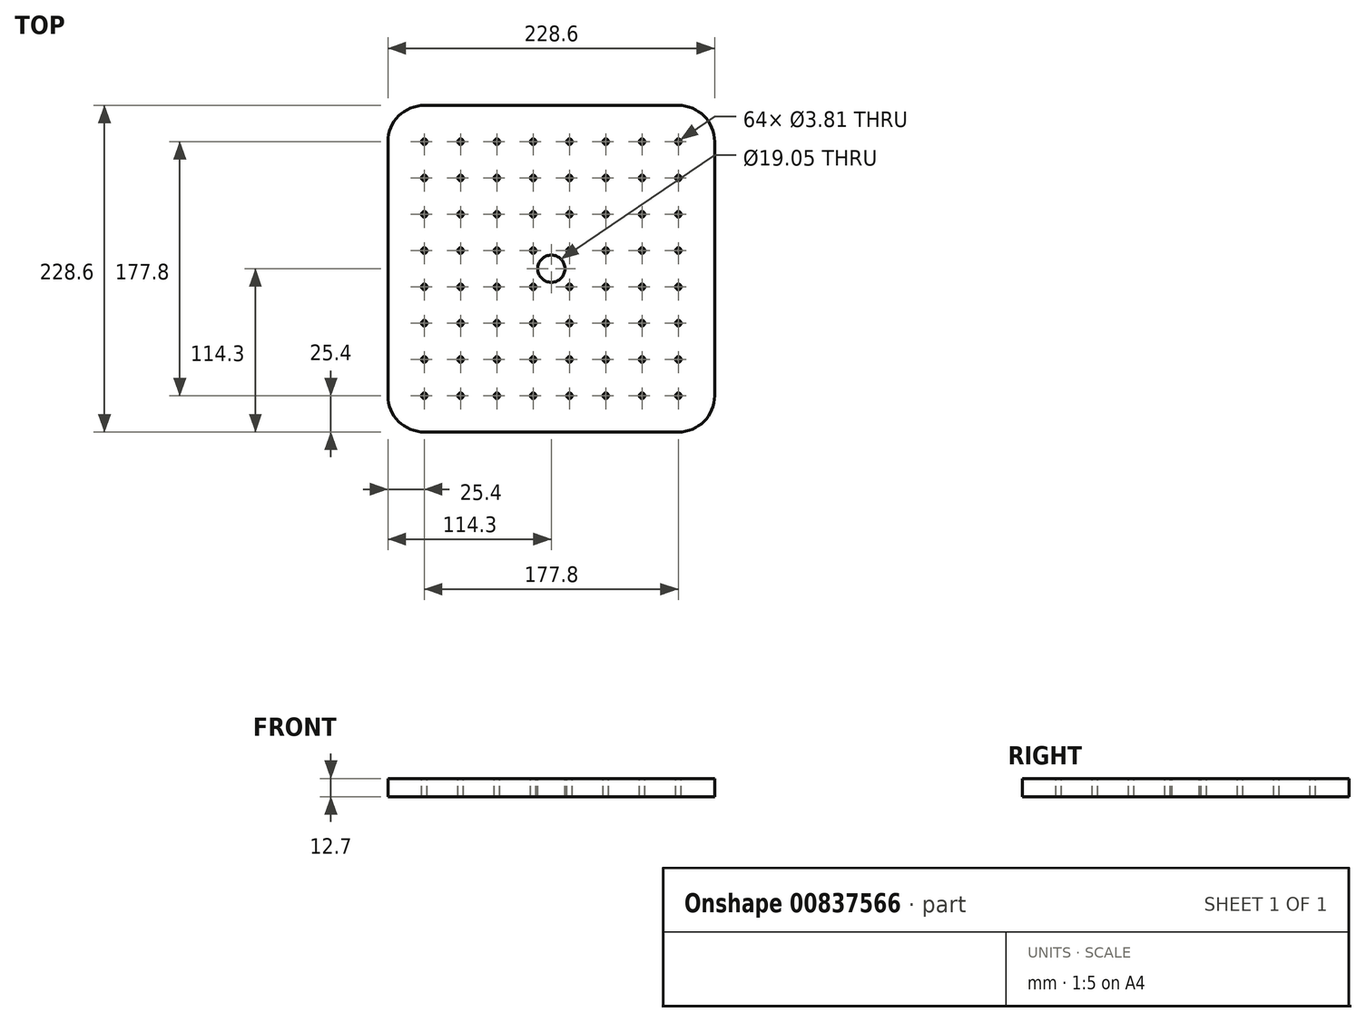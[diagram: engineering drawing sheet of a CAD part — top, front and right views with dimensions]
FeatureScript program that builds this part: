
annotation { "Feature Type Name" : "Feature", "Feature Type Description" : "" }
export const myFeature = defineFeature(function(context is Context, id is Id, definition is map)
    precondition{}
    {
        {
            var Q0;
            Q0=qCreatedBy(makeId("Top.planeOp"),FACE);
            var sketch = newSketch(context, id + "F0", { "sketchPlane" : qUnion([Q0])});
            skLineSegment(sketch, "E0.bottom", {"start": v(88.9, 114.3) * mm, "end": v(-88.9, 114.3) * mm});
            skLineSegment(sketch, "E0.top", {"start": v(88.9, -114.3) * mm, "end": v(-88.9, -114.3) * mm});
            skLineSegment(sketch, "E0.left", {"start": v(114.3, 88.9) * mm, "end": v(114.3, -88.9) * mm});
            skLineSegment(sketch, "E0.right", {"start": v(-114.3, 88.9) * mm, "end": v(-114.3, -88.9) * mm});
            skPoint(sketch, "E0.middle", {"position": v(0, 0) * mm});
            skCircle(sketch, "E1", {"center": v(-88.9, 88.9) * mm, "radius": 1.9 * mm});
            skLineSegment(sketch, "E2", {"start": v(-88.9, 88.9) * mm, "end": v(-88.9, 114.3) * mm, "construction": true});
            skLineSegment(sketch, "E3", {"start": v(-114.3, 88.9) * mm, "end": v(-88.9, 88.9) * mm, "construction": true});
            skCircle(sketch, "E4.0.1.0", {"center": v(-88.9, 63.5) * mm, "radius": 1.9 * mm});
            skCircle(sketch, "E4.1.0.0", {"center": v(-63.5, 88.9) * mm, "radius": 1.9 * mm});
            skCircle(sketch, "E4.1.1.0", {"center": v(-63.5, 63.5) * mm, "radius": 1.9 * mm});
            skCircle(sketch, "E4.2.0.0", {"center": v(-38.1, 88.9) * mm, "radius": 1.9 * mm});
            skCircle(sketch, "E4.2.1.0", {"center": v(-38.1, 63.5) * mm, "radius": 1.9 * mm});
            skLineSegment(sketch, "E4.direction1", {"start": v(-88.9, 88.9) * mm, "end": v(-63.5, 88.9) * mm, "construction": true});
            skLineSegment(sketch, "E4.direction2", {"start": v(-88.9, 88.9) * mm, "end": v(-88.9, 63.5) * mm, "construction": true});
            skCircle(sketch, "E5.0.0.2", {"center": v(-88.9, 38.1) * mm, "radius": 1.9 * mm});
            skCircle(sketch, "E5.0.0.3", {"center": v(-88.9, 12.7) * mm, "radius": 1.9 * mm});
            skCircle(sketch, "E5.0.0.4", {"center": v(-88.9, -12.7) * mm, "radius": 1.9 * mm});
            skCircle(sketch, "E5.0.0.5", {"center": v(-88.9, -38.1) * mm, "radius": 1.9 * mm});
            skCircle(sketch, "E5.0.0.6", {"center": v(-88.9, -63.5) * mm, "radius": 1.9 * mm});
            skCircle(sketch, "E5.0.0.7", {"center": v(-88.9, -88.9) * mm, "radius": 1.9 * mm});
            skCircle(sketch, "E5.0.1.2", {"center": v(-63.5, 38.1) * mm, "radius": 1.9 * mm});
            skCircle(sketch, "E5.0.1.3", {"center": v(-63.5, 12.7) * mm, "radius": 1.9 * mm});
            skCircle(sketch, "E5.0.1.4", {"center": v(-63.5, -12.7) * mm, "radius": 1.9 * mm});
            skCircle(sketch, "E5.0.1.5", {"center": v(-63.5, -38.1) * mm, "radius": 1.9 * mm});
            skCircle(sketch, "E5.0.1.6", {"center": v(-63.5, -63.5) * mm, "radius": 1.9 * mm});
            skCircle(sketch, "E5.0.1.7", {"center": v(-63.5, -88.9) * mm, "radius": 1.9 * mm});
            skCircle(sketch, "E5.0.2.2", {"center": v(-38.1, 38.1) * mm, "radius": 1.9 * mm});
            skCircle(sketch, "E5.0.2.3", {"center": v(-38.1, 12.7) * mm, "radius": 1.9 * mm});
            skCircle(sketch, "E5.0.2.4", {"center": v(-38.1, -12.7) * mm, "radius": 1.9 * mm});
            skCircle(sketch, "E5.0.2.5", {"center": v(-38.1, -38.1) * mm, "radius": 1.9 * mm});
            skCircle(sketch, "E5.0.2.6", {"center": v(-38.1, -63.5) * mm, "radius": 1.9 * mm});
            skCircle(sketch, "E5.0.2.7", {"center": v(-38.1, -88.9) * mm, "radius": 1.9 * mm});
            skCircle(sketch, "E6.0.3.0", {"center": v(-12.7, 88.9) * mm, "radius": 1.9 * mm});
            skCircle(sketch, "E6.0.3.1", {"center": v(-12.7, 63.5) * mm, "radius": 1.9 * mm});
            skCircle(sketch, "E6.0.3.2", {"center": v(-12.7, 38.1) * mm, "radius": 1.9 * mm});
            skCircle(sketch, "E6.0.3.3", {"center": v(-12.7, 12.7) * mm, "radius": 1.9 * mm});
            skCircle(sketch, "E6.0.3.4", {"center": v(-12.7, -12.7) * mm, "radius": 1.9 * mm});
            skCircle(sketch, "E6.0.3.5", {"center": v(-12.7, -38.1) * mm, "radius": 1.9 * mm});
            skCircle(sketch, "E6.0.3.6", {"center": v(-12.7, -63.5) * mm, "radius": 1.9 * mm});
            skCircle(sketch, "E6.0.3.7", {"center": v(-12.7, -88.9) * mm, "radius": 1.9 * mm});
            skCircle(sketch, "E6.0.4.0", {"center": v(12.7, 88.9) * mm, "radius": 1.9 * mm});
            skCircle(sketch, "E6.0.4.1", {"center": v(12.7, 63.5) * mm, "radius": 1.9 * mm});
            skCircle(sketch, "E6.0.4.2", {"center": v(12.7, 38.1) * mm, "radius": 1.9 * mm});
            skCircle(sketch, "E6.0.4.3", {"center": v(12.7, 12.7) * mm, "radius": 1.9 * mm});
            skCircle(sketch, "E6.0.4.4", {"center": v(12.7, -12.7) * mm, "radius": 1.9 * mm});
            skCircle(sketch, "E6.0.4.5", {"center": v(12.7, -38.1) * mm, "radius": 1.9 * mm});
            skCircle(sketch, "E6.0.4.6", {"center": v(12.7, -63.5) * mm, "radius": 1.9 * mm});
            skCircle(sketch, "E6.0.4.7", {"center": v(12.7, -88.9) * mm, "radius": 1.9 * mm});
            skCircle(sketch, "E6.0.5.0", {"center": v(38.1, 88.9) * mm, "radius": 1.9 * mm});
            skCircle(sketch, "E6.0.5.1", {"center": v(38.1, 63.5) * mm, "radius": 1.9 * mm});
            skCircle(sketch, "E6.0.5.2", {"center": v(38.1, 38.1) * mm, "radius": 1.9 * mm});
            skCircle(sketch, "E6.0.5.3", {"center": v(38.1, 12.7) * mm, "radius": 1.9 * mm});
            skCircle(sketch, "E6.0.5.4", {"center": v(38.1, -12.7) * mm, "radius": 1.9 * mm});
            skCircle(sketch, "E6.0.5.5", {"center": v(38.1, -38.1) * mm, "radius": 1.9 * mm});
            skCircle(sketch, "E6.0.5.6", {"center": v(38.1, -63.5) * mm, "radius": 1.9 * mm});
            skCircle(sketch, "E6.0.5.7", {"center": v(38.1, -88.9) * mm, "radius": 1.9 * mm});
            skCircle(sketch, "E6.0.6.0", {"center": v(63.5, 88.9) * mm, "radius": 1.9 * mm});
            skCircle(sketch, "E6.0.6.1", {"center": v(63.5, 63.5) * mm, "radius": 1.9 * mm});
            skCircle(sketch, "E6.0.6.2", {"center": v(63.5, 38.1) * mm, "radius": 1.9 * mm});
            skCircle(sketch, "E6.0.6.3", {"center": v(63.5, 12.7) * mm, "radius": 1.9 * mm});
            skCircle(sketch, "E6.0.6.4", {"center": v(63.5, -12.7) * mm, "radius": 1.9 * mm});
            skCircle(sketch, "E6.0.6.5", {"center": v(63.5, -38.1) * mm, "radius": 1.9 * mm});
            skCircle(sketch, "E6.0.6.6", {"center": v(63.5, -63.5) * mm, "radius": 1.9 * mm});
            skCircle(sketch, "E6.0.6.7", {"center": v(63.5, -88.9) * mm, "radius": 1.9 * mm});
            skCircle(sketch, "E6.0.7.0", {"center": v(88.9, 88.9) * mm, "radius": 1.9 * mm});
            skCircle(sketch, "E6.0.7.1", {"center": v(88.9, 63.5) * mm, "radius": 1.9 * mm});
            skCircle(sketch, "E6.0.7.2", {"center": v(88.9, 38.1) * mm, "radius": 1.9 * mm});
            skCircle(sketch, "E6.0.7.3", {"center": v(88.9, 12.7) * mm, "radius": 1.9 * mm});
            skCircle(sketch, "E6.0.7.4", {"center": v(88.9, -12.7) * mm, "radius": 1.9 * mm});
            skCircle(sketch, "E6.0.7.5", {"center": v(88.9, -38.1) * mm, "radius": 1.9 * mm});
            skCircle(sketch, "E6.0.7.6", {"center": v(88.9, -63.5) * mm, "radius": 1.9 * mm});
            skCircle(sketch, "E6.0.7.7", {"center": v(88.9, -88.9) * mm, "radius": 1.9 * mm});
            skPoint(sketch, "E7.visualSharp", {"position": v(-114.3, 114.3) * mm});
            skArc(sketch, "E7.filletArc", {"start": v(-88.9, 114.3) * mm, "mid": v(-106.86, 106.86) * mm, "end": v(-114.3, 88.9) * mm});
            skPoint(sketch, "E8.visualSharp", {"position": v(114.3, 114.3) * mm});
            skArc(sketch, "E8.filletArc", {"start": v(114.3, 88.9) * mm, "mid": v(106.86, 106.86) * mm, "end": v(88.9, 114.3) * mm});
            skPoint(sketch, "E9.visualSharp", {"position": v(114.3, -114.3) * mm});
            skArc(sketch, "E9.filletArc", {"start": v(88.9, -114.3) * mm, "mid": v(106.86, -106.86) * mm, "end": v(114.3, -88.9) * mm});
            skPoint(sketch, "E10.visualSharp", {"position": v(-114.3, -114.3) * mm});
            skArc(sketch, "E10.filletArc", {"start": v(-114.3, -88.9) * mm, "mid": v(-106.86, -106.86) * mm, "end": v(-88.9, -114.3) * mm});
            skLineSegment(sketch, "E11", {"start": v(-114.3, 3.17) * mm, "end": v(114.3, 3.18) * mm});
            skLineSegment(sketch, "E12", {"start": v(-3.17, 3.17) * mm, "end": v(-3.18, 114.3) * mm});
            skLineSegment(sketch, "E13", {"start": v(3.18, 3.17) * mm, "end": v(3.17, 114.3) * mm});
            skLineSegment(sketch, "E14.bottom", {"start": v(3.18, 3.17) * mm, "end": v(-3.18, 3.17) * mm, "construction": true});
            skLineSegment(sketch, "E14.top", {"start": v(3.18, -3.18) * mm, "end": v(-3.17, -3.18) * mm, "construction": true});
            skLineSegment(sketch, "E14.left", {"start": v(3.17, 3.17) * mm, "end": v(3.18, -3.18) * mm, "construction": true});
            skLineSegment(sketch, "E14.right", {"start": v(-3.18, 3.18) * mm, "end": v(-3.17, -3.18) * mm, "construction": true});
            skLineSegment(sketch, "E15.MirrorCS", {"start": v(-3.17, -3.17) * mm, "end": v(-3.17, -114.3) * mm});
            skLineSegment(sketch, "E16.MirrorCS", {"start": v(3.17, -3.17) * mm, "end": v(3.18, -114.3) * mm});
            skLineSegment(sketch, "E17.MirrorCS", {"start": v(-114.3, -3.18) * mm, "end": v(114.3, -3.17) * mm});
            skCircle(sketch, "E18", {"center": v(0, 0) * mm, "radius": 9.53 * mm});
            skSolve(sketch);
        }
        {
            var Q0;
            Q0 = qSketchRegion(id + "F0", true);
            extrude(context, id + "F1", {"entities" : qUnion([Q0]), "oppositeDirection" : true, "depth" : 12.7 * mm, "offsetDistance" : 25.4 * mm});
        }
    });
